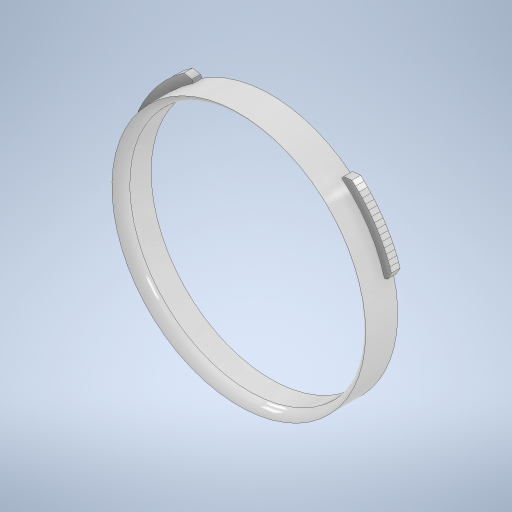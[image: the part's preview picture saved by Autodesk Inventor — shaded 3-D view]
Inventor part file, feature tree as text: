
AUTODESK INVENTOR PART (.ipt)
format: ipt  version: 2023 (Build 270158000, 158)  size: 4,739,584 bytes
history: native  units: mm
features: other x3, extrude x2, sketch x1, fillet x1
ambient origin geometry x8: Origin, YZ Plane, XZ Plane, XY Plane, X Axis, Y Axis, Z Axis, Center Point
bodies: Solido1 (feature_tree)
feature tree (7):
  other  "Sony_E-Mount_Body_Cap"
  sketch  "Schizzo1"
  extrude  "Estrusione1"  Depth=5.5mm TaperAngle=0.0deg
  extrude  "Estrusione2"  Depth=1.5mm TaperAngle=0.0deg
  fillet  "Raccordo1"  Radius=2.0mm
  other  "Composto1"
  other  "Superf1"
